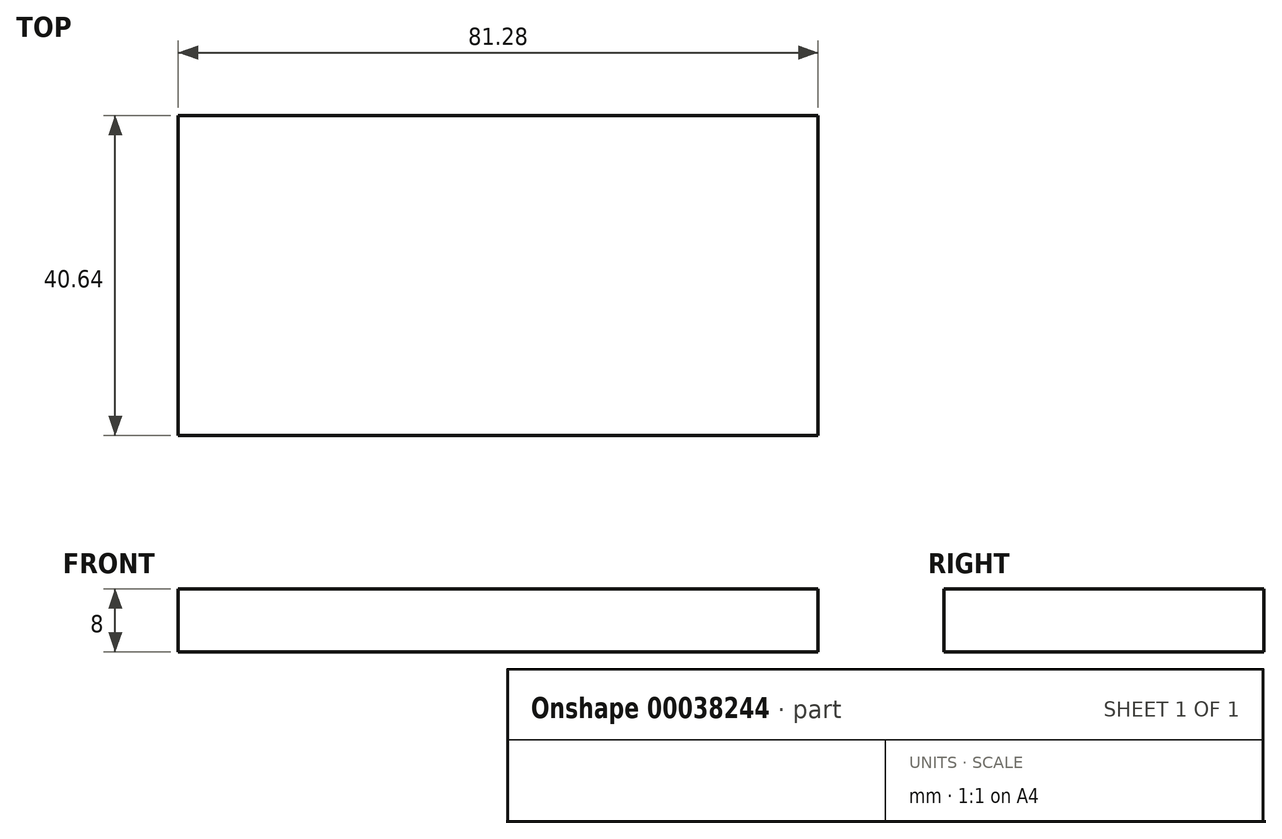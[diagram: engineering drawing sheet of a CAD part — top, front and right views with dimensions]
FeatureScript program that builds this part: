
annotation { "Feature Type Name" : "Feature", "Feature Type Description" : "" }
export const myFeature = defineFeature(function(context is Context, id is Id, definition is map)
    precondition{}
    {
        {
            var Q0;
            Q0=qCreatedBy(makeId("Top.planeOp"),FACE);
            var sketch = newSketch(context, id + "F0", { "sketchPlane" : qUnion([Q0])});
            skLineSegment(sketch, "E0", {"start": v(-39.44, 0) * mm, "end": v(41.84, 0) * mm});
            skLineSegment(sketch, "E1", {"start": v(-39.44, 0) * mm, "end": v(-39.44, 40.64) * mm});
            skLineSegment(sketch, "E2", {"start": v(-39.44, 40.64) * mm, "end": v(41.84, 40.64) * mm});
            skLineSegment(sketch, "E3", {"start": v(41.84, 40.64) * mm, "end": v(41.84, 0) * mm});
            skSolve(sketch);
        }
        {
            var Q0;
            Q0=makeQuery(id+"F0.imprint","IMPRINT",FACE,{"disambiguationData":[TD([[makeQuery(id+"F0.imprint","IMPRINT",EDGE,{"derivedFrom":sQuery(id+"F0.wireOp",EDGE,"E0")}),1.0]])]});
            extrude(context, id + "F1", {"entities" : qUnion([Q0]), "depth" : 8 * mm});
        }
    });
